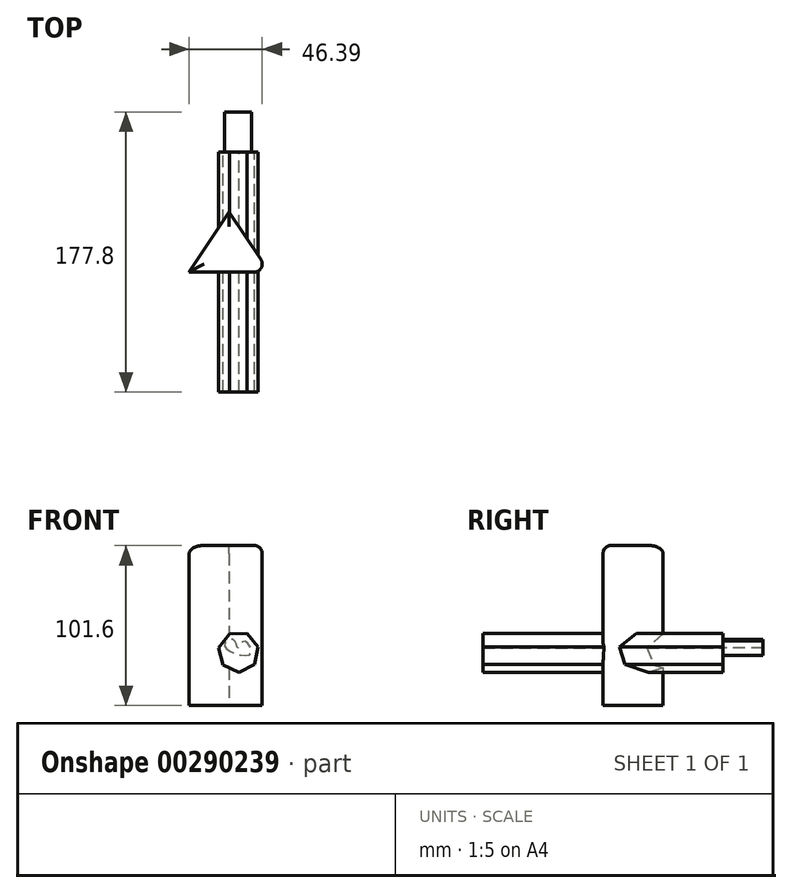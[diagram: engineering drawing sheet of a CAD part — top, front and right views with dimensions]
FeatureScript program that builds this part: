
annotation { "Feature Type Name" : "Feature", "Feature Type Description" : "" }
export const myFeature = defineFeature(function(context is Context, id is Id, definition is map)
    precondition{}
    {
        {
            var Q0;
            Q0=qCreatedBy(makeId("Top.planeOp"),FACE);
            var sketch = newSketch(context, id + "F0", { "sketchPlane" : qUnion([Q0])});
            skLineSegment(sketch, "E0", {"start": v(0, 0) * mm, "end": v(-25.4, -38.1) * mm});
            skLineSegment(sketch, "E1", {"start": v(-25.4, -38.1) * mm, "end": v(25.4, -38.1) * mm});
            skLineSegment(sketch, "E2", {"start": v(25.4, -38.1) * mm, "end": v(0, 0) * mm});
            skSolve(sketch);
        }
        {
            var Q0;
            Q0 = qSketchRegion(id + "F0", true);
            extrude(context, id + "F1", {"entities" : qUnion([Q0]), "endBound" : BoundingType.SYMMETRIC, "depth" : 101.6 * mm});
        }
        {
            var Q0;
            Q0=makeQuery(id+"F1.opExtrude","SWEPT_FACE",FACE,{"disambiguationData":[OSD([sQuery(id+"F0.wireOp",EDGE,"E1")])]});
            var sketch = newSketch(context, id + "F2", { "sketchPlane" : qUnion([Q0])});
            skCircle(sketch, "E3.cCircle", {"center": v(5.92, -16.8) * mm, "radius": 11.66 * mm, "construction": true});
            skLineSegment(sketch, "E3.0", {"start": v(-6.74, -14.18) * mm, "end": v(0.08, -5.26) * mm});
            skLineSegment(sketch, "E3.1", {"start": v(0.08, -5.26) * mm, "end": v(11.3, -5.04) * mm});
            skLineSegment(sketch, "E3.2", {"start": v(11.3, -5.04) * mm, "end": v(18.48, -13.68) * mm});
            skLineSegment(sketch, "E3.3", {"start": v(18.48, -13.68) * mm, "end": v(16.2, -24.67) * mm});
            skLineSegment(sketch, "E3.4", {"start": v(16.2, -24.67) * mm, "end": v(6.18, -29.74) * mm});
            skLineSegment(sketch, "E3.5", {"start": v(6.18, -29.74) * mm, "end": v(-4.03, -25.07) * mm});
            skLineSegment(sketch, "E3.6", {"start": v(-4.03, -25.07) * mm, "end": v(-6.74, -14.18) * mm});
            skPoint(sketch, "E3.0.midPoint", {"position": v(-3.33, -9.72) * mm});
            skSolve(sketch);
        }
        {
            var Q0;
            Q0=makeQuery(id+"F2.imprint","IMPRINT",FACE,{"disambiguationData":[TD([[makeQuery(id+"F2.imprint","IMPRINT",EDGE,{"derivedFrom":sQuery(id+"F2.wireOp",EDGE,"E3.0")}),-1.0]])]});
            extrude(context, id + "F3", {"entities" : qUnion([Q0]), "operationType" : NewBodyOperationType.ADD, "endBound" : BoundingType.SYMMETRIC, "depth" : 152.4 * mm});
        }
        {
            var Q0;
            Q0=makeQuery(id+"F3.opExtrude","CAP_FACE",FACE,{"disambiguationData":[OSD([sQuery(id+"F2.wireOp",EDGE,"E3.0"),sQuery(id+"F2.wireOp",EDGE,"E3.1"),sQuery(id+"F2.wireOp",EDGE,"E3.2"),sQuery(id+"F2.wireOp",EDGE,"E3.3"),sQuery(id+"F2.wireOp",EDGE,"E3.4"),sQuery(id+"F2.wireOp",EDGE,"E3.5"),sQuery(id+"F2.wireOp",EDGE,"E3.6")])],"isStart":true});
            var sketch = newSketch(context, id + "F4", { "sketchPlane" : qUnion([Q0])});
            skPoint(sketch, "E4.3.internal.snap0", {"position": v(-5.7, -5.15) * mm});
            skFitSpline(sketch, "E4", {"points": [v(2.92, -13) * mm, v(-13.7, -17.96) * mm, v(-9.5, -9.94) * mm, v(-5.7, -14.14) * mm, v(-2.62, -8.99) * mm, v(2.92, -13) * mm]});
            skSolve(sketch);
        }
        {
            var Q0;
            Q0=makeQuery(id+"F4.imprint","IMPRINT",FACE,{"disambiguationData":[TD([[makeQuery(id+"F4.imprint","IMPRINT",EDGE,{"derivedFrom":sQuery(id+"F4.wireOp",EDGE,"E4")}),-1.0]])]});
            extrude(context, id + "F5", {"entities" : qUnion([Q0]), "operationType" : NewBodyOperationType.ADD, "depth" : 25.4 * mm});
        }
        {
            var Q0;
            Q0=makeQuery(id+"F1.opExtrude","SWEPT_EDGE",EDGE,{"disambiguationData":[OSD([sQuery(id+"F0.wireOp",EDGE,"E1"),sQuery(id+"F0.wireOp",EDGE,"E2")])]});
            var Q1;
            Q1=makeQuery(id+"F1.opExtrude","CAP_EDGE",EDGE,{"disambiguationData":[OSD([sQuery(id+"F0.wireOp",EDGE,"E2")])],"isStart":false});
            var Q2;
            Q2=makeQuery(id+"F1.opExtrude","CAP_EDGE",EDGE,{"disambiguationData":[OSD([sQuery(id+"F0.wireOp",EDGE,"E0")])],"isStart":false});
            var Q3;
            Q3=makeQuery(id+"F1.opExtrude","CAP_FACE",FACE,{"disambiguationData":[OSD([sQuery(id+"F0.wireOp",EDGE,"E0"),sQuery(id+"F0.wireOp",EDGE,"E1"),sQuery(id+"F0.wireOp",EDGE,"E2")])],"isStart":false});
            fillet(context, id + "F6", {"entities" : qUnion([Q0, Q1, Q2, Q3]), "radius" : 5.08 * mm, "tangentPropagation" : true, "allowEdgeOverflow" : false});
        }
    });
